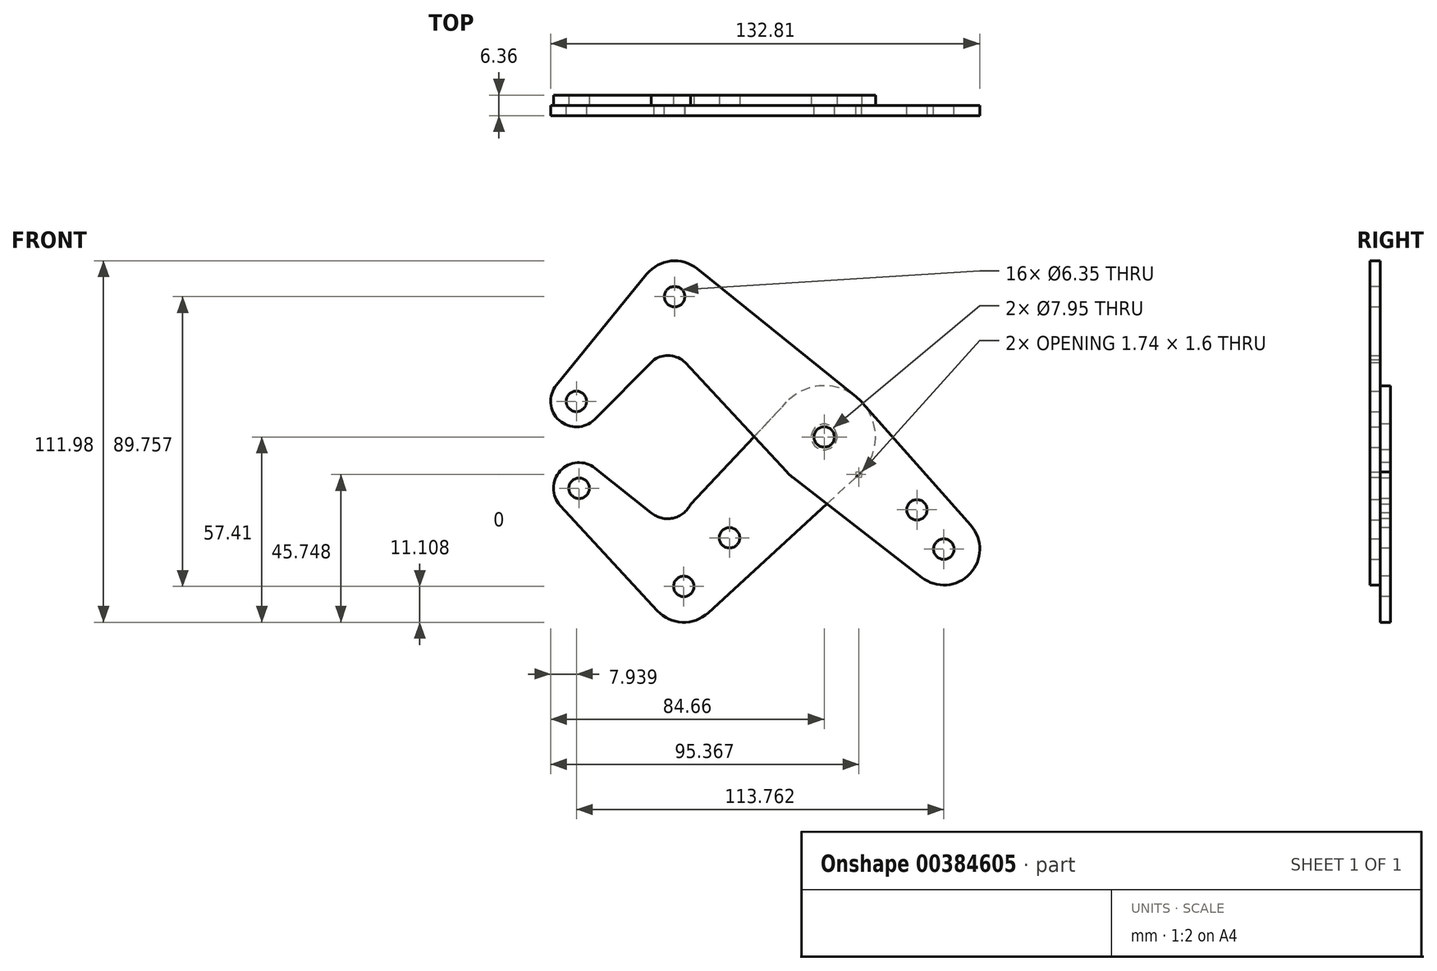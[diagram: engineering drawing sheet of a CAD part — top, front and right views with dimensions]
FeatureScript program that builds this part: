
annotation { "Feature Type Name" : "Feature", "Feature Type Description" : "" }
export const myFeature = defineFeature(function(context is Context, id is Id, definition is map)
    precondition{}
    {
        {
            var Q0;
            Q0=qCreatedBy(makeId("Front.planeOp"),FACE);
            var sketch = newSketch(context, id + "F0", { "sketchPlane" : qUnion([Q0])});
            skCircle(sketch, "E0", {"center": v(0, 0) * mm, "radius": 15.88 * mm});
            skCircle(sketch, "E1", {"center": v(0, 0) * mm, "radius": 3.98 * mm});
            skCircle(sketch, "E2", {"center": v(37.04, -34.76) * mm, "radius": 11.11 * mm});
            skLineSegment(sketch, "E3", {"start": v(11.9, 10.5) * mm, "end": v(45.37, -27.41) * mm});
            skLineSegment(sketch, "E4", {"start": v(30.23, -43.54) * mm, "end": v(-9.73, -12.54) * mm});
            skCircle(sketch, "E5", {"center": v(28.7, -22.59) * mm, "radius": 3.17 * mm});
            skCircle(sketch, "E6", {"center": v(37.04, -34.76) * mm, "radius": 3.18 * mm});
            skCircle(sketch, "E7", {"center": v(-46.3, 43.46) * mm, "radius": 11.11 * mm});
            skLineSegment(sketch, "E8", {"start": v(-39.33, 52.1) * mm, "end": v(9.97, 12.36) * mm});
            skLineSegment(sketch, "E9", {"start": v(-46.3, 43.46) * mm, "end": v(-76.72, 11.04) * mm, "construction": true});
            skCircle(sketch, "E10", {"center": v(-76.72, 11.04) * mm, "radius": 7.94 * mm});
            skLineSegment(sketch, "E11", {"start": v(-54.93, 50.46) * mm, "end": v(-82.88, 16.05) * mm});
            skArc(sketch, "E12", {"start": v(-52.66, 24) * mm, "mid": v(-47.64, 25.2) * mm, "end": v(-42.95, 23.06) * mm});
            skLineSegment(sketch, "E13", {"start": v(-42.95, 23.06) * mm, "end": v(-11.66, -10.78) * mm});
            skLineSegment(sketch, "E14", {"start": v(-52.66, 24) * mm, "end": v(-71.1, 5.45) * mm});
            skCircle(sketch, "E15", {"center": v(-76.72, 11.04) * mm, "radius": 3.18 * mm});
            skCircle(sketch, "E16", {"center": v(-46.3, 43.46) * mm, "radius": 3.18 * mm});
            skCircle(sketch, "E17", {"center": v(0, 0) * mm, "radius": 3.18 * mm});
            skLineSegment(sketch, "E18", {"start": v(0, 0) * mm, "end": v(-43.46, -46.3) * mm, "construction": true});
            skLineSegment(sketch, "E19", {"start": v(-43.46, -46.3) * mm, "end": v(-75.87, -15.88) * mm, "construction": true});
            skCircle(sketch, "E20", {"center": v(-43.46, -46.3) * mm, "radius": 11.11 * mm});
            skCircle(sketch, "E21", {"center": v(-75.87, -15.88) * mm, "radius": 7.94 * mm});
            skLineSegment(sketch, "E22", {"start": v(11.58, -10.86) * mm, "end": v(-35.94, -54.49) * mm});
            skLineSegment(sketch, "E23", {"start": v(-51.62, -53.84) * mm, "end": v(-81.7, -21.27) * mm});
            skArc(sketch, "E24", {"start": v(-41.42, -20.93) * mm, "mid": v(-46.87, -25.15) * mm, "end": v(-53.57, -23.52) * mm});
            skLineSegment(sketch, "E25", {"start": v(-70.92, -9.68) * mm, "end": v(-53.57, -23.52) * mm});
            skLineSegment(sketch, "E26", {"start": v(-41.42, -20.93) * mm, "end": v(-11.58, 10.86) * mm});
            skLineSegment(sketch, "E27", {"start": v(-46.3, 43.46) * mm, "end": v(37.04, -34.76) * mm, "construction": true});
            skCircle(sketch, "E28", {"center": v(-75.87, -15.88) * mm, "radius": 3.18 * mm});
            skCircle(sketch, "E29", {"center": v(-43.46, -46.3) * mm, "radius": 3.18 * mm});
            skCircle(sketch, "E30", {"center": v(-29.32, -31.24) * mm, "radius": 3.18 * mm});
            skSolve(sketch);
        }
        {
            var Q0;
            {var subQ3=sQuery(id+"F0.wireOp",EDGE,"E8");Q0=makeQuery(id+"F0.imprint","IMPRINT",FACE,{"disambiguationData":[TD([[makeQuery(id+"F0.imprint","IMPRINT",EDGE,{"derivedFrom":subQ3}),-1.0]])]});}
            var Q1;
            Q1=makeQuery(id+"F0.imprint","IMPRINT",FACE,{"disambiguationData":[TD([[makeQuery(id+"F0.imprint","IMPRINT",EDGE,{"derivedFrom":sQuery(id+"F0.wireOp",EDGE,"E15")}),-1.0]])]});
            var Q2;
            Q2=makeQuery(id+"F0.imprint","IMPRINT",FACE,{"disambiguationData":[TD([[makeQuery(id+"F0.imprint","IMPRINT",EDGE,{"derivedFrom":sQuery(id+"F0.wireOp",EDGE,"E16")}),-1.0]])]});
            var Q3;
            Q3=makeQuery(id+"F0.imprint","IMPRINT",FACE,{"disambiguationData":[TD([[makeQuery(id+"F0.imprint","IMPRINT",EDGE,{"derivedFrom":sQuery(id+"F0.wireOp",EDGE,"E1")}),-1.0]])]});
            var Q4;
            {var subQ0=sQuery(id+"F0.wireOp",EDGE,"E3");Q4=makeQuery(id+"F0.imprint","IMPRINT",FACE,{"disambiguationData":[TD([[makeQuery(id+"F0.imprint","IMPRINT",EDGE,{"derivedFrom":subQ0}),-1.0]])]});}
            var Q5;
            {var subQ0=sQuery(id+"F0.wireOp",EDGE,"E13");var subQ1=sQuery(id+"F0.wireOp",EDGE,"E0");var subQ2=makeQuery(id+"F0.imprint","INTERSECT",VERTEX,{"derivedFrom":[subQ1,subQ0]});Q5=makeQuery(id+"F0.imprint","IMPRINT",FACE,{"disambiguationData":[TD([[makeQuery(id+"F0.imprint","IMPRINT",EDGE,{"disambiguationData":[TD([[subQ2,1.0]])],"derivedFrom":subQ1}),-1.0]])]});}
            var Q6;
            {var subQ0=sQuery(id+"F0.wireOp",EDGE,"E4");var subQ1=sQuery(id+"F0.wireOp",EDGE,"E0");var subQ2=makeQuery(id+"F0.imprint","INTERSECT",VERTEX,{"derivedFrom":[subQ1,subQ0]});Q6=makeQuery(id+"F0.imprint","IMPRINT",FACE,{"disambiguationData":[TD([[makeQuery(id+"F0.imprint","IMPRINT",EDGE,{"disambiguationData":[TD([[subQ2,-1.0]])],"derivedFrom":subQ1}),-1.0]])]});}
            var Q7;
            Q7=makeQuery(id+"F0.imprint","IMPRINT",FACE,{"disambiguationData":[TD([[makeQuery(id+"F0.imprint","IMPRINT",EDGE,{"derivedFrom":sQuery(id+"F0.wireOp",EDGE,"E6")}),-1.0]])]});
            var Q8;
            Q8=makeQuery(id+"F0.imprint","IMPRINT",FACE,{"disambiguationData":[TD([[makeQuery(id+"F0.imprint","IMPRINT",EDGE,{"derivedFrom":sQuery(id+"F0.wireOp",EDGE,"E1")}),1.0]])]});
            extrude(context, id + "F1", {"entities" : qUnion([Q0, Q1, Q2, Q3, Q4, Q5, Q6, Q7, Q8]), "depth" : 3.17 * mm});
        }
        {
            var Q0;
            Q0=makeQuery(id+"F0.imprint","IMPRINT",FACE,{"disambiguationData":[TD([[makeQuery(id+"F0.imprint","IMPRINT",EDGE,{"derivedFrom":sQuery(id+"F0.wireOp",EDGE,"E28")}),-1.0]])]});
            var Q1;
            {var subQ5=sQuery(id+"F0.wireOp",EDGE,"E23");Q1=makeQuery(id+"F0.imprint","IMPRINT",FACE,{"disambiguationData":[TD([[makeQuery(id+"F0.imprint","IMPRINT",EDGE,{"derivedFrom":subQ5}),-1.0]])]});}
            var Q2;
            Q2=makeQuery(id+"F0.imprint","IMPRINT",FACE,{"disambiguationData":[TD([[makeQuery(id+"F0.imprint","IMPRINT",EDGE,{"derivedFrom":sQuery(id+"F0.wireOp",EDGE,"E29")}),-1.0]])]});
            var Q3;
            Q3=makeQuery(id+"F0.imprint","IMPRINT",FACE,{"disambiguationData":[TD([[makeQuery(id+"F0.imprint","IMPRINT",EDGE,{"derivedFrom":sQuery(id+"F0.wireOp",EDGE,"E1")}),-1.0]])]});
            var Q4;
            {var subQ0=sQuery(id+"F0.wireOp",EDGE,"E13");var subQ1=sQuery(id+"F0.wireOp",EDGE,"E0");var subQ2=makeQuery(id+"F0.imprint","INTERSECT",VERTEX,{"derivedFrom":[subQ1,subQ0]});Q4=makeQuery(id+"F0.imprint","IMPRINT",FACE,{"disambiguationData":[TD([[makeQuery(id+"F0.imprint","IMPRINT",EDGE,{"disambiguationData":[TD([[subQ2,1.0]])],"derivedFrom":subQ1}),-1.0]])]});}
            var Q5;
            {var subQ0=sQuery(id+"F0.wireOp",EDGE,"E4");var subQ1=sQuery(id+"F0.wireOp",EDGE,"E0");var subQ2=makeQuery(id+"F0.imprint","INTERSECT",VERTEX,{"derivedFrom":[subQ1,subQ0]});Q5=makeQuery(id+"F0.imprint","IMPRINT",FACE,{"disambiguationData":[TD([[makeQuery(id+"F0.imprint","IMPRINT",EDGE,{"disambiguationData":[TD([[subQ2,-1.0]])],"derivedFrom":subQ1}),-1.0]])]});}
            extrude(context, id + "F2", {"entities" : qUnion([Q0, Q1, Q2, Q3, Q4, Q5]), "oppositeDirection" : true, "depth" : 3.17 * mm});
        }
    });
